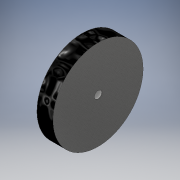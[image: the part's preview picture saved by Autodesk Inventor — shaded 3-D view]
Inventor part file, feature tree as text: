
AUTODESK INVENTOR PART (.ipt)
format: ipt  version: 2019 (Build 230136000, 136)  size: 108,544 bytes
history: native  units: in
note: dims shown in document units (in); Inventor stores cm internally (conversion verified against a paired STEP export)
features: extrude x1, sketch x1
ambient origin geometry x8: Origin, YZ Plane, XZ Plane, XY Plane, X Axis, Y Axis, Z Axis, Center Point
bodies: Solid1 (feature_tree)
feature tree (2):
  extrude  "Extrusion1"  Depth=0.3543in
  sketch  "Sketch1"  dims[d0=1.9685in d1=0.1575in d2=0.3543in d3=0.0in]
